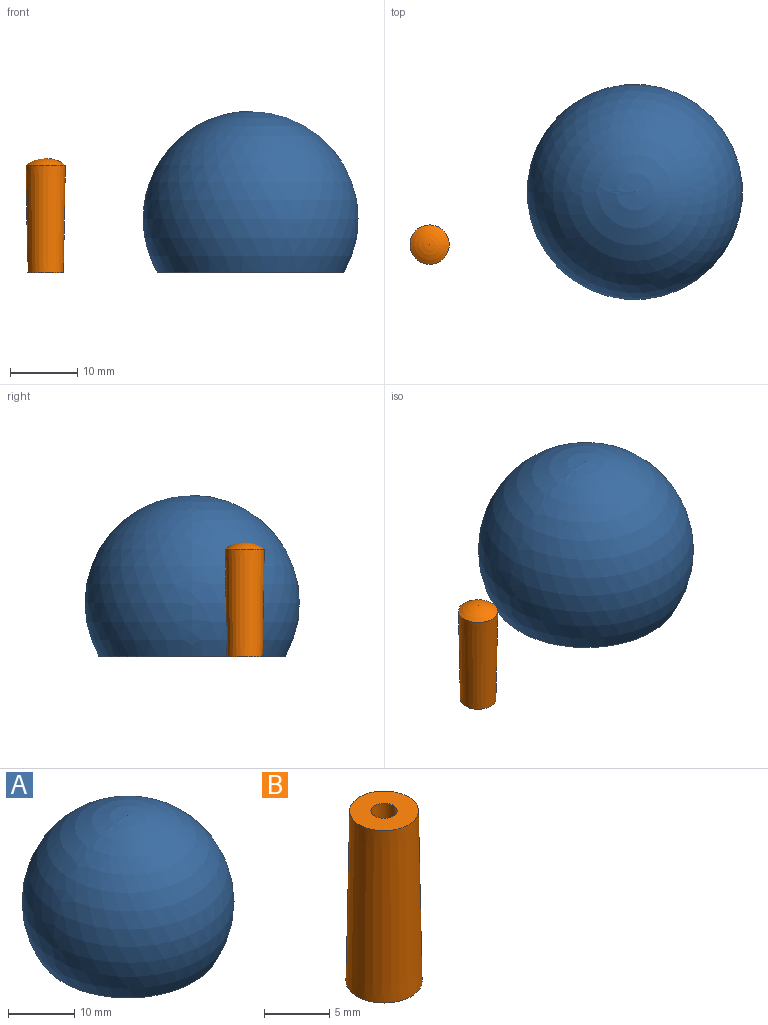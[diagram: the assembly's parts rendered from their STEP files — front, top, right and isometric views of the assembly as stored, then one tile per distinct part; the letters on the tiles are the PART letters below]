
ASSEMBLY  parts=2 mates=1
PART A: 8 faces, bbox 32x32x24 mm
  f0: sphere r=14.8mm, area 2033.2mm2, adj f1,f5
  f1: cone r=5.18mm half-angle=45deg, axis (0,0,1), area 95.3mm2, adj f0,f2
  f2: cone r=2.31mm half-angle=1deg, axis (0,0,-1), area 296mm2, adj f1,f3
  f3: plane 5.29x5.29mm, normal (0,0,-1), area 18.8mm2, adj f2,f6
  f4: sphere r=16mm, area 2412.7mm2, adj f5
  f5: plane 27.71x27.71mm, normal (0,0,-1), area 116.1mm2, adj f0,f4
  f6: cylinder r=1mm len=3mm, axis (0,0,-1), area 18.8mm2, adj f3,f7
  f7: plane 2x2mm, normal (0,0,-1), area 3.1mm2, adj f6
PART B: 5 faces, bbox 5.8x5.8x17 mm
  f0: cone r=2.64mm half-angle=1deg, axis (0,0,-1), area 280mm2, adj f1,f2
  f1: plane 5.29x5.29mm, normal (0,0,1), area 18.8mm2, adj f0,f3
  f2: sphere r=4.78mm, area 30mm2, adj f0
  f3: cylinder r=1mm len=3mm, axis (0,0,1), area 18.8mm2, adj f1,f4
  f4: plane 2x2mm, normal (0,0,1), area 3.1mm2, adj f3
PLACE A t=(8.86,1.71,-0.03)mm
PLACE B rot(axis=(1,0,0),180deg) t=(-21.64,-6.12,-0.03)mm
MATE planar A.f1 <-> B.f0  axis (0,0,-1) through (8.86,1.71,-0.03)mm
